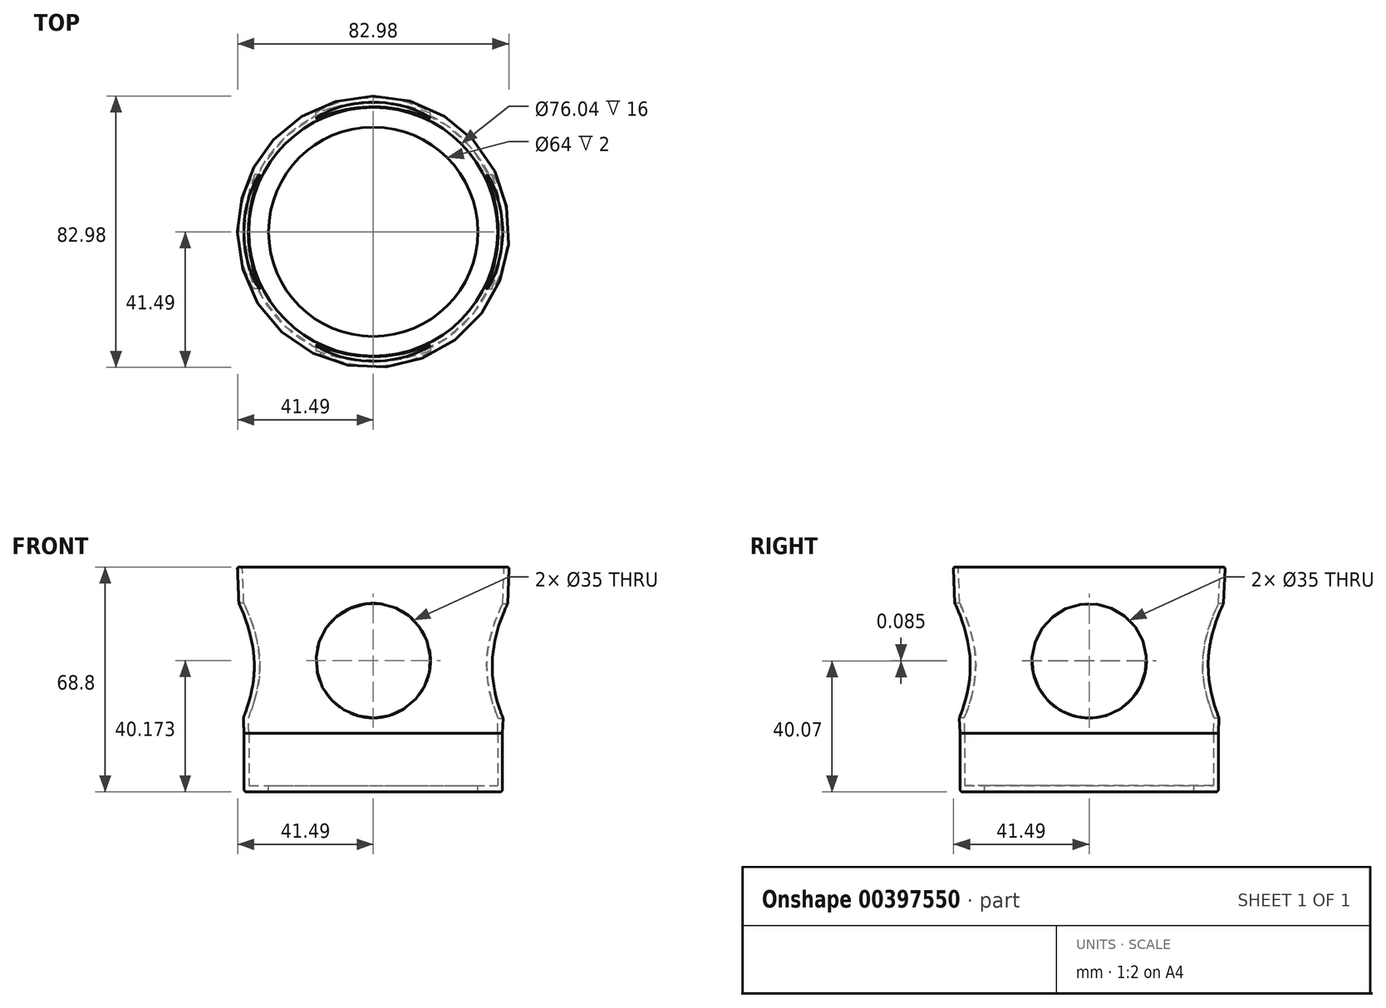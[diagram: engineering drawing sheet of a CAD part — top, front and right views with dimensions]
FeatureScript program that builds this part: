
annotation { "Feature Type Name" : "Feature", "Feature Type Description" : "" }
export const myFeature = defineFeature(function(context is Context, id is Id, definition is map)
    precondition{}
    {
        {
            var Q0;
            Q0=qCreatedBy(makeId("Front.planeOp"),FACE);
            var sketch = newSketch(context, id + "F0", { "sketchPlane" : qUnion([Q0])});
            skLineSegment(sketch, "E0.bottom", {"start": v(0, 0) * mm, "end": v(-38.02, 0) * mm});
            skLineSegment(sketch, "E0.top", {"start": v(0, 2) * mm, "end": v(-38.02, 2) * mm});
            skLineSegment(sketch, "E0.left", {"start": v(0, 0) * mm, "end": v(0, 2) * mm});
            skLineSegment(sketch, "E0.right", {"start": v(-38.02, 0) * mm, "end": v(-38.02, 2) * mm});
            skLineSegment(sketch, "E1.bottom", {"start": v(-38.02, 0) * mm, "end": v(-39.52, 0) * mm});
            skLineSegment(sketch, "E1.top", {"start": v(-38.02, 18) * mm, "end": v(-39.52, 18) * mm});
            skLineSegment(sketch, "E1.right", {"start": v(-39.52, 0) * mm, "end": v(-39.52, 18) * mm});
            skLineSegment(sketch, "E2", {"start": v(0, 2) * mm, "end": v(0, 68.8) * mm});
            skLineSegment(sketch, "E3", {"start": v(0, 68.8) * mm, "end": v(-40.02, 68.8) * mm});
            skLineSegment(sketch, "E4", {"start": v(-38.02, 18) * mm, "end": v(-38.02, 2) * mm});
            skLineSegment(sketch, "E5", {"start": v(-38.02, 18) * mm, "end": v(-40.02, 68.8) * mm});
            skLineSegment(sketch, "E6", {"start": v(-40.02, 68.8) * mm, "end": v(-41.52, 68.8) * mm});
            skLineSegment(sketch, "E7", {"start": v(-41.52, 68.8) * mm, "end": v(-39.52, 18) * mm});
            skLineSegment(sketch, "E8", {"start": v(0, 0) * mm, "end": v(-35.5, 0) * mm});
            skLineSegment(sketch, "E9.bottom", {"start": v(-35.5, 0) * mm, "end": v(-34, 0) * mm});
            skLineSegment(sketch, "E9.top", {"start": v(-35.5, -20) * mm, "end": v(-34, -20) * mm});
            skLineSegment(sketch, "E9.left", {"start": v(-35.5, 0) * mm, "end": v(-35.5, -20) * mm});
            skLineSegment(sketch, "E9.right", {"start": v(-34, 0) * mm, "end": v(-34, -20) * mm});
            skLineSegment(sketch, "E10", {"start": v(-34, 0) * mm, "end": v(-34, -2) * mm});
            skLineSegment(sketch, "E11", {"start": v(-34, 0) * mm, "end": v(-32, 0) * mm});
            skLineSegment(sketch, "E12", {"start": v(-32, 0) * mm, "end": v(-34, -2) * mm});
            skLineSegment(sketch, "E13", {"start": v(-39.52, 0) * mm, "end": v(-39.52, 2) * mm});
            skLineSegment(sketch, "E14", {"start": v(-39.52, 0) * mm, "end": v(-42.02, 0) * mm});
            skLineSegment(sketch, "E15", {"start": v(-42.02, 0) * mm, "end": v(-39.52, 2) * mm});
            skSolve(sketch);
        }
        {
            var Q0;
            Q0=makeQuery(id+"F0.imprint","IMPRINT",FACE,{"disambiguationData":[TD([[makeQuery(id+"F0.imprint","IMPRINT",EDGE,{"derivedFrom":sQuery(id+"F0.wireOp",EDGE,"E1.top")}),-1.0]])]});
            var Q1;
            Q1=makeQuery(id+"F0.imprint","IMPRINT",FACE,{"disambiguationData":[TD([[makeQuery(id+"F0.imprint","IMPRINT",EDGE,{"derivedFrom":sQuery(id+"F0.wireOp",EDGE,"E0.right")}),1.0]])]});
            var Q2;
            Q2=makeQuery(id+"F0.imprint","IMPRINT",FACE,{"disambiguationData":[TD([[makeQuery(id+"F0.imprint","IMPRINT",EDGE,{"derivedFrom":sQuery(id+"F0.wireOp",EDGE,"E13")}),1.0]])]});
            var Q3;
            Q3=makeQuery(id+"F0.imprint","IMPRINT",FACE,{"disambiguationData":[TD([[makeQuery(id+"F0.imprint","IMPRINT",EDGE,{"derivedFrom":sQuery(id+"F0.wireOp",EDGE,"E10")}),1.0]])]});
            var Q4;
            Q4=makeQuery(id+"F0.imprint","IMPRINT",FACE,{"disambiguationData":[TD([[makeQuery(id+"F0.imprint","IMPRINT",EDGE,{"derivedFrom":sQuery(id+"F0.wireOp",EDGE,"E9.bottom")}),-1.0]])]});
            var Q5;
            Q5=makeQuery(id+"F0.imprint","IMPRINT",FACE,{"disambiguationData":[TD([[makeQuery(id+"F0.imprint","IMPRINT",EDGE,{"derivedFrom":sQuery(id+"F0.wireOp",EDGE,"E0.bottom")}),-1.0]])]});
            var Q6;
            Q6=sQuery(id+"F0.wireOp",EDGE,"E2");
            revolve(context, id + "F1", {"entities" : qUnion([Q0, Q1, Q2, Q3, Q4, Q5]), "axis" : qUnion([Q6]), "revolveType" : RevolveType.FULL});
        }
        {
            var Q0;
            Q0=qCreatedBy(makeId("Top.planeOp"),FACE);
            var sketch = newSketch(context, id + "F2", { "sketchPlane" : qUnion([Q0])});
            skPoint(sketch, "E16", {"position": v(0, 0) * mm});
            skSolve(sketch);
        }
        {
            var Q0;
            Q0=sQuery(id+"F2.wireOp",VERTEX,"E16");
            var Q1;
            Q1=makeQuery(id+"F1.opRevolve","SWEPT_BODY",BODY,{"disambiguationData":[OSD([sQuery(id+"F0.wireOp",EDGE,"E0.bottom"),sQuery(id+"F0.wireOp",EDGE,"E0.top"),sQuery(id+"F0.wireOp",EDGE,"E0.left"),sQuery(id+"F0.wireOp",EDGE,"E1.bottom"),sQuery(id+"F0.wireOp",EDGE,"E1.right"),sQuery(id+"F0.wireOp",EDGE,"E4"),sQuery(id+"F0.wireOp",EDGE,"E5"),sQuery(id+"F0.wireOp",EDGE,"E6"),sQuery(id+"F0.wireOp",EDGE,"E7"),sQuery(id+"F0.wireOp",EDGE,"E8"),sQuery(id+"F0.wireOp",EDGE,"E9.top"),sQuery(id+"F0.wireOp",EDGE,"E9.left"),sQuery(id+"F0.wireOp",EDGE,"E9.right"),sQuery(id+"F0.wireOp",EDGE,"E12"),sQuery(id+"F0.wireOp",EDGE,"E14"),sQuery(id+"F0.wireOp",EDGE,"E15")])]});
            hole(context, id + "F3", {"style" : HoleStyle.SIMPLE, "endStyle" : HoleEndStyle.THROUGH, "oppositeDirection" : true, "holeDiameter" : 64 * mm, "isTappedThrough" : true, "tappedDepth" : 12 * mm, "tapClearance" : 3, "locations" : qUnion([Q0]), "scope" : qUnion([Q1]), "startStyle" : HoleStartStyle.SKETCH});
        }
        {
            var Q0;
            Q0=makeQuery(id+"F1.opRevolve","SWEPT_EDGE",EDGE,{"disambiguationData":[OSD([sQuery(id+"F0.wireOp",EDGE,"E6"),sQuery(id+"F0.wireOp",EDGE,"E7")])]});
            var Q1;
            Q1=makeQuery(id+"F1.opRevolve","SWEPT_EDGE",EDGE,{"disambiguationData":[OSD([sQuery(id+"F0.wireOp",EDGE,"E3"),sQuery(id+"F0.wireOp",EDGE,"E5"),sQuery(id+"F0.wireOp",EDGE,"E6")])]});
            fillet(context, id + "F4", {"entities" : qUnion([Q0, Q1]), "radius" : .5 * mm, "tangentPropagation" : true, "allowEdgeOverflow" : false});
        }
        {
            var Q0;
            Q0=makeQuery(id+"F1.opRevolve","SWEPT_EDGE",EDGE,{"disambiguationData":[OSD([sQuery(id+"F0.wireOp",EDGE,"E14"),sQuery(id+"F0.wireOp",EDGE,"E15")])]});
            fillet(context, id + "F5", {"entities" : qUnion([Q0]), "radius" : 1 * mm, "tangentPropagation" : true, "rho" : 0.5, "crossSection" : FilletCrossSection.CONIC, "allowEdgeOverflow" : false});
        }
        {
            var Q0;
            Q0=qCreatedBy(makeId("Front.planeOp"),FACE);
            var sketch = newSketch(context, id + "F6", { "sketchPlane" : qUnion([Q0])});
            skPoint(sketch, "E17", {"position": v(0, 40.17) * mm});
            skSolve(sketch);
        }
        {
            var Q0;
            Q0=sQuery(id+"F6.wireOp",VERTEX,"E17");
            var Q1;
            Q1=makeQuery(id+"F1.opRevolve","SWEPT_BODY",BODY,{"disambiguationData":[OSD([sQuery(id+"F0.wireOp",EDGE,"E0.bottom"),sQuery(id+"F0.wireOp",EDGE,"E0.top"),sQuery(id+"F0.wireOp",EDGE,"E0.left"),sQuery(id+"F0.wireOp",EDGE,"E1.bottom"),sQuery(id+"F0.wireOp",EDGE,"E1.right"),sQuery(id+"F0.wireOp",EDGE,"E4"),sQuery(id+"F0.wireOp",EDGE,"E5"),sQuery(id+"F0.wireOp",EDGE,"E6"),sQuery(id+"F0.wireOp",EDGE,"E7"),sQuery(id+"F0.wireOp",EDGE,"E8"),sQuery(id+"F0.wireOp",EDGE,"E9.top"),sQuery(id+"F0.wireOp",EDGE,"E9.left"),sQuery(id+"F0.wireOp",EDGE,"E9.right"),sQuery(id+"F0.wireOp",EDGE,"E12"),sQuery(id+"F0.wireOp",EDGE,"E14"),sQuery(id+"F0.wireOp",EDGE,"E15")])]});
            hole(context, id + "F7", {"style" : HoleStyle.SIMPLE, "endStyle" : HoleEndStyle.THROUGH, "holeDiameter" : 35 * mm, "isTappedThrough" : true, "tappedDepth" : 12 * mm, "tapClearance" : 3, "locations" : qUnion([Q0]), "scope" : qUnion([Q1]), "startStyle" : HoleStartStyle.SKETCH});
        }
        {
            var Q0;
            Q0=sQuery(id+"F6.wireOp",VERTEX,"E17");
            var Q1;
            Q1=makeQuery(id+"F1.opRevolve","SWEPT_BODY",BODY,{"disambiguationData":[OSD([sQuery(id+"F0.wireOp",EDGE,"E0.bottom"),sQuery(id+"F0.wireOp",EDGE,"E0.top"),sQuery(id+"F0.wireOp",EDGE,"E0.left"),sQuery(id+"F0.wireOp",EDGE,"E1.bottom"),sQuery(id+"F0.wireOp",EDGE,"E1.right"),sQuery(id+"F0.wireOp",EDGE,"E4"),sQuery(id+"F0.wireOp",EDGE,"E5"),sQuery(id+"F0.wireOp",EDGE,"E6"),sQuery(id+"F0.wireOp",EDGE,"E7"),sQuery(id+"F0.wireOp",EDGE,"E8"),sQuery(id+"F0.wireOp",EDGE,"E9.top"),sQuery(id+"F0.wireOp",EDGE,"E9.left"),sQuery(id+"F0.wireOp",EDGE,"E9.right"),sQuery(id+"F0.wireOp",EDGE,"E12"),sQuery(id+"F0.wireOp",EDGE,"E14"),sQuery(id+"F0.wireOp",EDGE,"E15")])]});
            hole(context, id + "F8", {"style" : HoleStyle.SIMPLE, "endStyle" : HoleEndStyle.THROUGH, "oppositeDirection" : true, "holeDiameter" : 35 * mm, "isTappedThrough" : true, "tappedDepth" : 12 * mm, "tapClearance" : 3, "locations" : qUnion([Q0]), "scope" : qUnion([Q1]), "startStyle" : HoleStartStyle.SKETCH});
        }
        {
            var Q0;
            Q0=qCreatedBy(makeId("Right.planeOp"),FACE);
            var sketch = newSketch(context, id + "F9", { "sketchPlane" : qUnion([Q0])});
            skPoint(sketch, "E18", {"position": v(0, 40.15) * mm});
            skSolve(sketch);
        }
        {
            var Q0;
            Q0=sQuery(id+"F9.wireOp",VERTEX,"E18");
            var Q1;
            Q1=makeQuery(id+"F1.opRevolve","SWEPT_BODY",BODY,{"disambiguationData":[OSD([sQuery(id+"F0.wireOp",EDGE,"E0.bottom"),sQuery(id+"F0.wireOp",EDGE,"E0.top"),sQuery(id+"F0.wireOp",EDGE,"E0.left"),sQuery(id+"F0.wireOp",EDGE,"E1.bottom"),sQuery(id+"F0.wireOp",EDGE,"E1.right"),sQuery(id+"F0.wireOp",EDGE,"E4"),sQuery(id+"F0.wireOp",EDGE,"E5"),sQuery(id+"F0.wireOp",EDGE,"E6"),sQuery(id+"F0.wireOp",EDGE,"E7"),sQuery(id+"F0.wireOp",EDGE,"E8"),sQuery(id+"F0.wireOp",EDGE,"E9.top"),sQuery(id+"F0.wireOp",EDGE,"E9.left"),sQuery(id+"F0.wireOp",EDGE,"E9.right"),sQuery(id+"F0.wireOp",EDGE,"E12"),sQuery(id+"F0.wireOp",EDGE,"E14"),sQuery(id+"F0.wireOp",EDGE,"E15")])]});
            hole(context, id + "F10", {"style" : HoleStyle.SIMPLE, "endStyle" : HoleEndStyle.THROUGH, "holeDiameter" : 35 * mm, "isTappedThrough" : true, "tappedDepth" : 12 * mm, "tapClearance" : 3, "locations" : qUnion([Q0]), "scope" : qUnion([Q1]), "startStyle" : HoleStartStyle.SKETCH});
        }
        {
            var Q0;
            Q0=qCreatedBy(makeId("Right.planeOp"),FACE);
            var sketch = newSketch(context, id + "F11", { "sketchPlane" : qUnion([Q0])});
            skPoint(sketch, "E19", {"position": v(0, 40.07) * mm});
            skSolve(sketch);
        }
        {
            var Q0;
            Q0=sQuery(id+"F11.wireOp",VERTEX,"E19");
            var Q1;
            Q1=makeQuery(id+"F1.opRevolve","SWEPT_BODY",BODY,{"disambiguationData":[OSD([sQuery(id+"F0.wireOp",EDGE,"E0.bottom"),sQuery(id+"F0.wireOp",EDGE,"E0.top"),sQuery(id+"F0.wireOp",EDGE,"E0.left"),sQuery(id+"F0.wireOp",EDGE,"E1.bottom"),sQuery(id+"F0.wireOp",EDGE,"E1.right"),sQuery(id+"F0.wireOp",EDGE,"E4"),sQuery(id+"F0.wireOp",EDGE,"E5"),sQuery(id+"F0.wireOp",EDGE,"E6"),sQuery(id+"F0.wireOp",EDGE,"E7"),sQuery(id+"F0.wireOp",EDGE,"E8"),sQuery(id+"F0.wireOp",EDGE,"E9.top"),sQuery(id+"F0.wireOp",EDGE,"E9.left"),sQuery(id+"F0.wireOp",EDGE,"E9.right"),sQuery(id+"F0.wireOp",EDGE,"E12"),sQuery(id+"F0.wireOp",EDGE,"E14"),sQuery(id+"F0.wireOp",EDGE,"E15")])]});
            hole(context, id + "F12", {"style" : HoleStyle.SIMPLE, "endStyle" : HoleEndStyle.THROUGH, "oppositeDirection" : true, "holeDiameter" : 35 * mm, "isTappedThrough" : true, "tappedDepth" : 12 * mm, "tapClearance" : 3, "locations" : qUnion([Q0]), "scope" : qUnion([Q1]), "startStyle" : HoleStartStyle.SKETCH});
        }
    });
